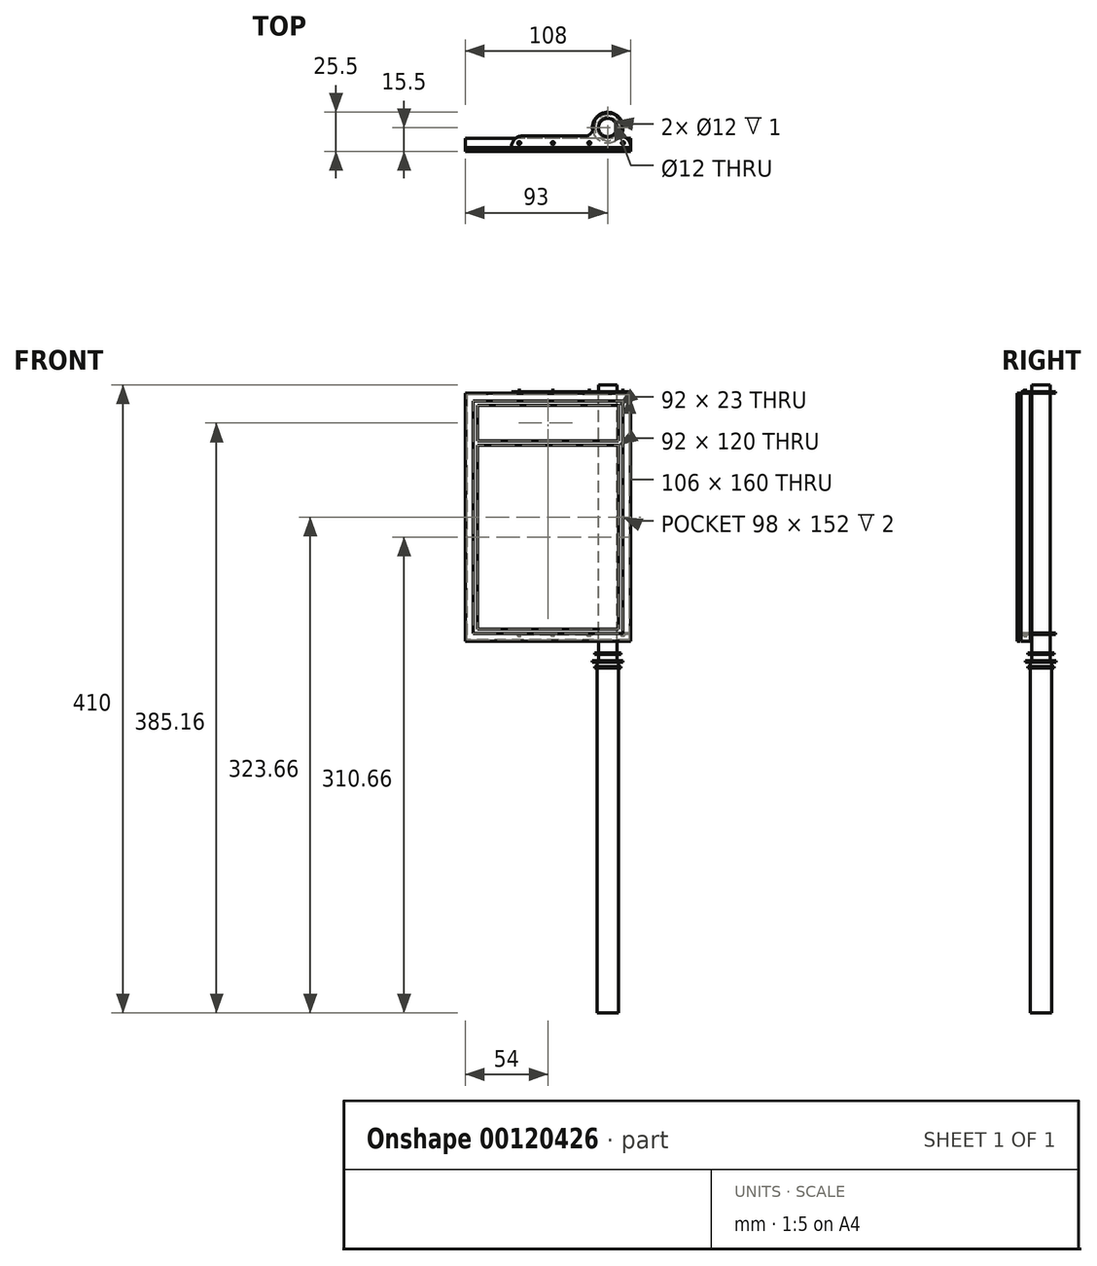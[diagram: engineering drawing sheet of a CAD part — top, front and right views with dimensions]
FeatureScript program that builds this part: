
annotation { "Feature Type Name" : "Feature", "Feature Type Description" : "" }
export const myFeature = defineFeature(function(context is Context, id is Id, definition is map)
    precondition{}
    {
        {
            var Q0;
            Q0=qCreatedBy(makeId("Front.planeOp"),FACE);
            var sketch = newSketch(context, id + "F0", { "sketchPlane" : qUnion([Q0])});
            skLineSegment(sketch, "E0.bottom", {"start": v(54, -81) * mm, "end": v(-54, -81) * mm});
            skLineSegment(sketch, "E0.top", {"start": v(54, 81) * mm, "end": v(-54, 81) * mm});
            skLineSegment(sketch, "E0.left", {"start": v(54, -81) * mm, "end": v(54, 81) * mm});
            skLineSegment(sketch, "E0.right", {"start": v(-54, -81) * mm, "end": v(-54, 81) * mm});
            skPoint(sketch, "E0.middle", {"position": v(0, 0) * mm});
            skLineSegment(sketch, "E1.0", {"start": v(49, 76) * mm, "end": v(-49, 76) * mm});
            skLineSegment(sketch, "E1.1", {"start": v(49, -76) * mm, "end": v(49, 76) * mm});
            skLineSegment(sketch, "E1.2", {"start": v(49, -76) * mm, "end": v(-49, -76) * mm});
            skLineSegment(sketch, "E1.3", {"start": v(-49, -76) * mm, "end": v(-49, 76) * mm});
            skLineSegment(sketch, "E2.bottom", {"start": v(46, -73) * mm, "end": v(-46, -73) * mm});
            skLineSegment(sketch, "E2.top", {"start": v(46, 50) * mm, "end": v(-46, 50) * mm});
            skLineSegment(sketch, "E2.right", {"start": v(-46, -73) * mm, "end": v(-46, 47) * mm});
            skPoint(sketch, "E2.middle", {"position": v(0, -11.5) * mm});
            skLineSegment(sketch, "E3.top", {"start": v(-46, 73) * mm, "end": v(46, 73) * mm});
            skLineSegment(sketch, "E3.left", {"start": v(-46, 50) * mm, "end": v(-46, 73) * mm});
            skLineSegment(sketch, "E3.right", {"start": v(46, 50) * mm, "end": v(46, 73) * mm});
            skLineSegment(sketch, "E4", {"start": v(-46, 47) * mm, "end": v(46, 47) * mm});
            skLineSegment(sketch, "E5", {"start": v(46, 47) * mm, "end": v(46, -73) * mm});
            skSolve(sketch);
        }
        {
            var Q0;
            Q0=makeQuery(id+"F0.imprint","IMPRINT",FACE,{"disambiguationData":[TD([[makeQuery(id+"F0.imprint","IMPRINT",EDGE,{"derivedFrom":sQuery(id+"F0.wireOp",EDGE,"E0.bottom")}),-1.0]])]});
            extrude(context, id + "F1", {"entities" : qUnion([Q0]), "oppositeDirection" : true, "depth" : 2 * mm});
        }
        {
            var Q0;
            Q0=makeQuery(id+"F0.imprint","IMPRINT",FACE,{"disambiguationData":[TD([[makeQuery(id+"F0.imprint","IMPRINT",EDGE,{"derivedFrom":sQuery(id+"F0.wireOp",EDGE,"E1.0")}),1.0]])]});
            extrude(context, id + "F2", {"entities" : qUnion([Q0]), "oppositeDirection" : true, "depth" : 1 * mm});
        }
        {
            var Q0;
            Q0=makeQuery(id+"F0.imprint","IMPRINT",FACE,{"disambiguationData":[TD([[makeQuery(id+"F0.imprint","IMPRINT",EDGE,{"derivedFrom":sQuery(id+"F0.wireOp",EDGE,"E2.top")}),-1.0]])]});
            extrude(context, id + "F3", {"entities" : qUnion([Q0]), "oppositeDirection" : true, "depth" : 1 * mm});
        }
        {
            var Q0;
            Q0=makeQuery(id+"F0.imprint","IMPRINT",FACE,{"disambiguationData":[TD([[makeQuery(id+"F0.imprint","IMPRINT",EDGE,{"derivedFrom":sQuery(id+"F0.wireOp",EDGE,"E2.bottom")}),-1.0]])]});
            extrude(context, id + "F4", {"entities" : qUnion([Q0]), "oppositeDirection" : true, "depth" : 1 * mm});
        }
        {
            var Q0;
            Q0=makeQuery(id+"F1.opExtrude","CAP_FACE",FACE,{"disambiguationData":[OSD([sQuery(id+"F0.wireOp",EDGE,"E0.bottom"),sQuery(id+"F0.wireOp",EDGE,"E0.top"),sQuery(id+"F0.wireOp",EDGE,"E0.left"),sQuery(id+"F0.wireOp",EDGE,"E0.right"),sQuery(id+"F0.wireOp",EDGE,"E1.0"),sQuery(id+"F0.wireOp",EDGE,"E1.1"),sQuery(id+"F0.wireOp",EDGE,"E1.2"),sQuery(id+"F0.wireOp",EDGE,"E1.3")])],"isStart":false});
            var sketch = newSketch(context, id + "F5", { "sketchPlane" : qUnion([Q0])});
            skLineSegment(sketch, "E6.bottom", {"start": v(-53, 80) * mm, "end": v(53, 80) * mm});
            skLineSegment(sketch, "E6.top", {"start": v(-53, -80) * mm, "end": v(53, -80) * mm});
            skLineSegment(sketch, "E6.left", {"start": v(-53, 80) * mm, "end": v(-53, -80) * mm});
            skLineSegment(sketch, "E6.right", {"start": v(53, 80) * mm, "end": v(53, -80) * mm});
            skSolve(sketch);
        }
        {
            var Q0;
            Q0 = qSketchRegion(id + "F5", true);
            extrude(context, id + "F6", {"entities" : qUnion([Q0]), "operationType" : NewBodyOperationType.ADD, "depth" : 0.5 * mm});
        }
        {
            var Q0;
            Q0=makeQuery(id+"F6.opExtrude","CAP_FACE",FACE,{"disambiguationData":[OSD([sQuery(id+"F5.wireOp",EDGE,"E6.bottom"),sQuery(id+"F5.wireOp",EDGE,"E6.top"),sQuery(id+"F5.wireOp",EDGE,"E6.left"),sQuery(id+"F5.wireOp",EDGE,"E6.right")])],"isStart":false});
            var sketch = newSketch(context, id + "F7", { "sketchPlane" : qUnion([Q0])});
            skLineSegment(sketch, "E7.bottom", {"start": v(-54, 81) * mm, "end": v(54, 81) * mm});
            skLineSegment(sketch, "E7.top", {"start": v(-54, -81) * mm, "end": v(54, -81) * mm});
            skLineSegment(sketch, "E7.left", {"start": v(-54, 81) * mm, "end": v(-54, -81) * mm});
            skLineSegment(sketch, "E7.right", {"start": v(54, 81) * mm, "end": v(54, -81) * mm});
            skPoint(sketch, "E7.middle", {"position": v(0, 0) * mm});
            skSolve(sketch);
        }
        {
            var Q0;
            Q0 = qSketchRegion(id + "F7", true);
            extrude(context, id + "F8", {"entities" : qUnion([Q0]), "operationType" : NewBodyOperationType.ADD, "depth" : 6 * mm});
        }
        {
            var Q0;
            Q0=makeQuery(id+"F8.opExtrude","SWEPT_FACE",FACE,{"disambiguationData":[OSD([sQuery(id+"F7.wireOp",EDGE,"E7.bottom")])]});
            var sketch = newSketch(context, id + "F9", { "sketchPlane" : qUnion([Q0])});
            skCircle(sketch, "E8", {"center": v(39, 15.5) * mm, "radius": 6 * mm});
            skLineSegment(sketch, "E9.bottom", {"start": v(-23.83, 2.5) * mm, "end": v(54, 2.5) * mm});
            skLineSegment(sketch, "E9.top", {"start": v(-16.83, 10) * mm, "end": v(15.17, 10) * mm});
            skLineSegment(sketch, "E9.left", {"start": v(-23.83, 2.5) * mm, "end": v(-23.83, 3) * mm});
            skLineSegment(sketch, "E9.right", {"start": v(54, 2.5) * mm, "end": v(54, 3) * mm});
            skLineSegment(sketch, "E10.trimOffspring", {"start": v(15.17, 10) * mm, "end": v(24.38, 10) * mm});
            skPoint(sketch, "E11.visualSharp", {"position": v(-8.57, 10) * mm});
            skPoint(sketch, "E12.visualSharp", {"position": v(8.57, 10) * mm});
            skPoint(sketch, "E13.visualSharp", {"position": v(-23.83, 10) * mm});
            skArc(sketch, "E13.filletArc", {"start": v(-16.83, 10) * mm, "mid": v(-21.78, 7.95) * mm, "end": v(-23.83, 3) * mm});
            skPoint(sketch, "E14.visualSharp", {"position": v(54, 10) * mm});
            skArc(sketch, "E14.filletArc", {"start": v(54, 3) * mm, "mid": v(53.14, 6.37) * mm, "end": v(50.76, 8.9) * mm});
            skArc(sketch, "E15", {"start": v(48.5, 13.94) * mm, "mid": v(39.62, 25.11) * mm, "end": v(29.37, 15.17) * mm});
            skLineSegment(sketch, "E16.trimOffspring", {"start": v(46.9, 10) * mm, "end": v(47, 10) * mm});
            skPoint(sketch, "E17.visualSharp", {"position": v(31.1, 10) * mm});
            skArc(sketch, "E17.filletArc", {"start": v(24.38, 10) * mm, "mid": v(27.97, 11.53) * mm, "end": v(29.37, 15.17) * mm});
            skArc(sketch, "E18.filletArc", {"start": v(48.5, 13.94) * mm, "mid": v(48.87, 11.08) * mm, "end": v(50.76, 8.9) * mm});
            skSolve(sketch);
        }
        {
            var Q0;
            Q0 = qSketchRegion(id + "F9", true);
            extrude(context, id + "F10", {"entities" : qUnion([Q0]), "depth" : 1 * mm});
        }
        {
            var Q0;
            Q0=makeQuery(id+"F10.opExtrude","SWEPT_BODY",BODY,{"disambiguationData":[OSD([sQuery(id+"F9.wireOp",EDGE,"E8"),sQuery(id+"F9.wireOp",EDGE,"E9.bottom"),sQuery(id+"F9.wireOp",EDGE,"E9.top"),sQuery(id+"F9.wireOp",EDGE,"E9.left"),sQuery(id+"F9.wireOp",EDGE,"E9.right"),sQuery(id+"F9.wireOp",EDGE,"ZpydVmt3-zrIR-JPEF-b4DS-NXEXzqit0afN"),sQuery(id+"F9.wireOp",EDGE,"E10.trimOffspring"),sQuery(id+"F9.wireOp",EDGE,"E11.filletArc"),sQuery(id+"F9.wireOp",EDGE,"E12.filletArc"),sQuery(id+"F9.wireOp",EDGE,"E13.filletArc"),sQuery(id+"F9.wireOp",EDGE,"E14.filletArc")])]});
            transform(context, id + "F11", {"entities" : qUnion([Q0]), "transformType" : TransformType.TRANSLATION_3D, "dx" : 0 * mm, "dy" : 0 * mm, "dz" : -163 * mm, "makeCopy" : true});
        }
        {
            var Q0;
            Q0=makeQuery(id+"F10.opExtrude","CAP_FACE",FACE,{"disambiguationData":[OSD([sQuery(id+"F9.wireOp",EDGE,"E8"),sQuery(id+"F9.wireOp",EDGE,"E9.bottom"),sQuery(id+"F9.wireOp",EDGE,"E9.top"),sQuery(id+"F9.wireOp",EDGE,"E9.left"),sQuery(id+"F9.wireOp",EDGE,"E9.right"),sQuery(id+"F9.wireOp",EDGE,"ZpydVmt3-zrIR-JPEF-b4DS-NXEXzqit0afN"),sQuery(id+"F9.wireOp",EDGE,"E10.trimOffspring"),sQuery(id+"F9.wireOp",EDGE,"E11.filletArc"),sQuery(id+"F9.wireOp",EDGE,"E12.filletArc"),sQuery(id+"F9.wireOp",EDGE,"E13.filletArc"),sQuery(id+"F9.wireOp",EDGE,"E14.filletArc")])],"isStart":false});
            var sketch = newSketch(context, id + "F12", { "sketchPlane" : qUnion([Q0])});
            skCircle(sketch, "E19", {"center": v(-18.83, 5.41) * mm, "radius": 1 * mm});
            skCircle(sketch, "E20", {"center": v(49, 5.41) * mm, "radius": 1 * mm});
            skCircle(sketch, "E21", {"center": v(3.17, 5.41) * mm, "radius": 1 * mm});
            skCircle(sketch, "E22", {"center": v(27, 5.41) * mm, "radius": 1 * mm});
            skSolve(sketch);
        }
        {
            var Q0;
            Q0 = qSketchRegion(id + "F12", true);
            extrude(context, id + "F13", {"entities" : qUnion([Q0]), "operationType" : NewBodyOperationType.ADD, "depth" : 1 * mm});
        }
        {
            var Q0;
            Q0=makeQuery(id+"F11.opPattern","COPY",FACE,{"derivedFrom":makeQuery(id+"F10.opExtrude","CAP_FACE",FACE,{"disambiguationData":[OSD([sQuery(id+"F9.wireOp",EDGE,"E8"),sQuery(id+"F9.wireOp",EDGE,"E9.bottom"),sQuery(id+"F9.wireOp",EDGE,"E9.top"),sQuery(id+"F9.wireOp",EDGE,"E9.left"),sQuery(id+"F9.wireOp",EDGE,"E9.right"),sQuery(id+"F9.wireOp",EDGE,"E10.trimOffspring"),sQuery(id+"F9.wireOp",EDGE,"E13.filletArc"),sQuery(id+"F9.wireOp",EDGE,"E14.filletArc"),sQuery(id+"F9.wireOp",EDGE,"E15"),sQuery(id+"F9.wireOp",EDGE,"E17.filletArc"),sQuery(id+"F9.wireOp",EDGE,"E18.filletArc")])],"isStart":true}),"instanceName":"1"});
            var sketch = newSketch(context, id + "F14", { "sketchPlane" : qUnion([Q0])});
            skCircle(sketch, "E23", {"center": v(-18.74, -5.39) * mm, "radius": 1 * mm});
            skCircle(sketch, "E24", {"center": v(3.26, -5.39) * mm, "radius": 1 * mm});
            skCircle(sketch, "E25", {"center": v(26.87, -5.39) * mm, "radius": 1 * mm});
            skCircle(sketch, "E26", {"center": v(48.87, -5.39) * mm, "radius": 1 * mm});
            skSolve(sketch);
        }
        {
            var Q0;
            Q0 = qSketchRegion(id + "F14", true);
            extrude(context, id + "F15", {"entities" : qUnion([Q0]), "operationType" : NewBodyOperationType.ADD, "depth" : 1 * mm});
        }
        {
            var Q0;
            Q0=makeQuery(id+"F9.imprint","IMPRINT",FACE,{"disambiguationData":[TD([[makeQuery(id+"F9.imprint","IMPRINT",EDGE,{"derivedFrom":sQuery(id+"F9.wireOp",EDGE,"E8")}),1.0]])]});
            extrude(context, id + "F16", {"entities" : qUnion([Q0]), "operationType" : NewBodyOperationType.ADD, "oppositeDirection" : true, "depth" : 180 * mm});
        }
        {
            var Q0;
            Q0=makeQuery(id+"F16.opExtrude","SWEPT_BODY",BODY,{"disambiguationData":[OSD([sQuery(id+"F9.wireOp",EDGE,"E8")])]});
            transform(context, id + "F17", {"entities" : qUnion([Q0]), "transformType" : TransformType.TRANSLATION_3D, "dx" : 0 * mm, "dy" : 0 * mm, "dz" : 5.34 * mm, "makeCopy" : false});
        }
        {
            var Q0;
            Q0=makeQuery(id+"F16.opExtrude","CAP_FACE",FACE,{"disambiguationData":[OSD([sQuery(id+"F9.wireOp",EDGE,"E8")])],"isStart":false});
            var sketch = newSketch(context, id + "F18", { "sketchPlane" : qUnion([Q0])});
            skCircle(sketch, "E27", {"center": v(39, -15.5) * mm, "radius": 7 * mm});
            skCircle(sketch, "E28", {"center": v(39, -15.5) * mm, "radius": 8.5 * mm});
            skCircle(sketch, "E29", {"center": v(39, -15.5) * mm, "radius": 10 * mm});
            skSolve(sketch);
        }
        {
            var Q0;
            Q0=makeQuery(id+"F18.imprint","IMPRINT",FACE,{"disambiguationData":[TD([[makeQuery(id+"F18.imprint","IMPRINT",EDGE,{"derivedFrom":makeQuery(id+"F16.opExtrude","CAP_EDGE",EDGE,{"disambiguationData":[OSD([sQuery(id+"F9.wireOp",EDGE,"E8")])],"isStart":false})}),-1.0]])]});
            var Q1;
            Q1=makeQuery(id+"F18.imprint","IMPRINT",FACE,{"disambiguationData":[TD([[makeQuery(id+"F18.imprint","IMPRINT",EDGE,{"derivedFrom":sQuery(id+"F18.wireOp",EDGE,"E27")}),1.0]])]});
            extrude(context, id + "F19", {"entities" : qUnion([Q0, Q1]), "operationType" : NewBodyOperationType.ADD, "depth" : 230 * mm});
        }
        {
            var Q0;
            Q0=makeQuery(id+"F18.imprint","IMPRINT",FACE,{"disambiguationData":[TD([[makeQuery(id+"F18.imprint","IMPRINT",EDGE,{"derivedFrom":sQuery(id+"F18.wireOp",EDGE,"E27")}),-1.0]])]});
            var Q1;
            Q1=makeQuery(id+"F18.imprint","IMPRINT",FACE,{"disambiguationData":[TD([[makeQuery(id+"F18.imprint","IMPRINT",EDGE,{"derivedFrom":sQuery(id+"F18.wireOp",EDGE,"E27")}),1.0]])]});
            extrude(context, id + "F20", {"entities" : qUnion([Q0, Q1]), "oppositeDirection" : true, "depth" : 1 * mm});
        }
        {
            var Q0;
            Q0=makeQuery(id+"F20.opExtrude","SWEPT_BODY",BODY,{"disambiguationData":[OSD([sQuery(id+"F9.wireOp",EDGE,"E8"),sQuery(id+"F18.wireOp",EDGE,"E28")])]});
            transform(context, id + "F21", {"entities" : qUnion([Q0]), "transformType" : TransformType.TRANSLATION_3D, "dx" : 0 * mm, "dy" : 0 * mm, "dz" : 4.1 * mm, "makeCopy" : false});
        }
        {
            var Q0;
            Q0=makeQuery(id+"F20.opExtrude","SWEPT_BODY",BODY,{"disambiguationData":[OSD([sQuery(id+"F9.wireOp",EDGE,"E8"),sQuery(id+"F18.wireOp",EDGE,"E28")])]});
            transform(context, id + "F22", {"entities" : qUnion([Q0]), "transformType" : TransformType.TRANSLATION_3D, "dx" : 0 * mm, "dy" : 0 * mm, "dz" : -9 * mm, "makeCopy" : true});
        }
        {
            var Q0;
            Q0=makeQuery(id+"F18.imprint","IMPRINT",FACE,{"disambiguationData":[TD([[makeQuery(id+"F18.imprint","IMPRINT",EDGE,{"derivedFrom":sQuery(id+"F18.wireOp",EDGE,"E27")}),-1.0]])]});
            var Q1;
            Q1=makeQuery(id+"F18.imprint","IMPRINT",FACE,{"disambiguationData":[TD([[makeQuery(id+"F18.imprint","IMPRINT",EDGE,{"derivedFrom":sQuery(id+"F18.wireOp",EDGE,"E28")}),-1.0]])]});
            var Q2;
            Q2=makeQuery(id+"F18.imprint","IMPRINT",FACE,{"disambiguationData":[TD([[makeQuery(id+"F18.imprint","IMPRINT",EDGE,{"derivedFrom":sQuery(id+"F18.wireOp",EDGE,"E27")}),1.0]])]});
            extrude(context, id + "F23", {"entities" : qUnion([Q0, Q1, Q2]), "operationType" : NewBodyOperationType.ADD, "depth" : 1 * mm});
        }
    });
